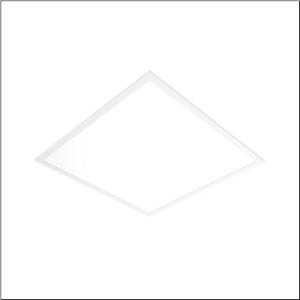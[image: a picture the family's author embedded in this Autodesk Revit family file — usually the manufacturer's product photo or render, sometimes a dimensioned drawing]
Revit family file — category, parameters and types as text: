
# Revit family: apollon_r__41_51mh12h72443_9ce2
name_source: partatom
category: Lighting Fixtures
units: mm (PartAtom-declared; Revit-internal decimal feet)

## family parameters
Cut with Voids When Loaded = No
Host = Face
Light Source = No
Part Type = Normal
Room Calculation Point = No
Round Connector Dimension = Use Diameter
Shared = No

## types (1)
- Apollon® 41 (1 x LED, 5000 lm, 38.5 W, 4000K)
    Apparent Load = 39 VA
    CIE Flux Codes = 61 87 97 100 100
    Color Rendering = 80
    Color Temperature = 4000K
    Default Elevation = 1800 mm
    Description = Apollon® 41, office luminaire, primary optical cover: prismatic diffuser, of PS, light emission: direct distribution, primary light characteristic: symmetric, installation type: lay-in mounting, LED, rated luminous flux: 5.000lm, luminous efficacy: 130lm/W, light colour: 840, colour temperature: 4000K, with terminal, 3-pole, mains connection: 220..240V, AC, 50/60Hz, rated input power: 38.5W, housing, of aluminium section, traffic white (RAL 9016), module: M600, length: 600mm, width: 600mm, height: 28mm, housing upper side, of sheet steel, protection rating (complete): IP20, protection rating (lamp compartment, on room side): IP40, insulation class (complete): insulation class II (safety insulation), certification: CE, ENEC, permissible operating ambient temperature: -25..+40°C, packaging unit: 1 piece
    Height = 0 mm  [stored 0 ft]
    Lamp = 1 x LED
    Lamp Light Flux = 5000 lm
    Lamp Power = 38.5 W
    Lamp count = 1
    Length = 600 mm
    Luminous efficacy = 130 lm/W
    Manufacturer = Siteco
    ModVariant = No
    Model = 51MH12H72443
    Mounting Place = Ceiling
    Mounting Type = Recessed
    Number of Poles = 1
    OnlyDefault = Yes
    Power Factor = 1
    Product Name = Apollon® 41
    Product group = office luminaire | ceiling recessed
    ProductGroupID = 401
    Protection Class = Protection class II
    Protection Degree = IP 20
    RLX_Detail_Level = 1
    RLX_Emergency_Light_Flux = 0 lm
    RLX_Emergency_Type = 0
    RLX_Emergency_Type_DB = No
    RlxData = <blob elided: 12197 chars, md5=d626e612>
    Socket = socket
    Standby Power = 0 W
    System Light Flux = 5000 lm
    System Power = 39 W
    Type Comments = Product without accessories
    Type Image = l_1291024.jpg
    URL = http://relux.com
    VarID = ---
    Voltage = 0 V
    Weight = 0.00 kg
    Width = 600 mm

note: [stored X ft] marks values corroborated as IEEE doubles in the binary element streams (Revit-internal decimal feet)

## geometry (parser evidence)
native form markers: Sweep x8
no freeform markers — native parametric forms only
